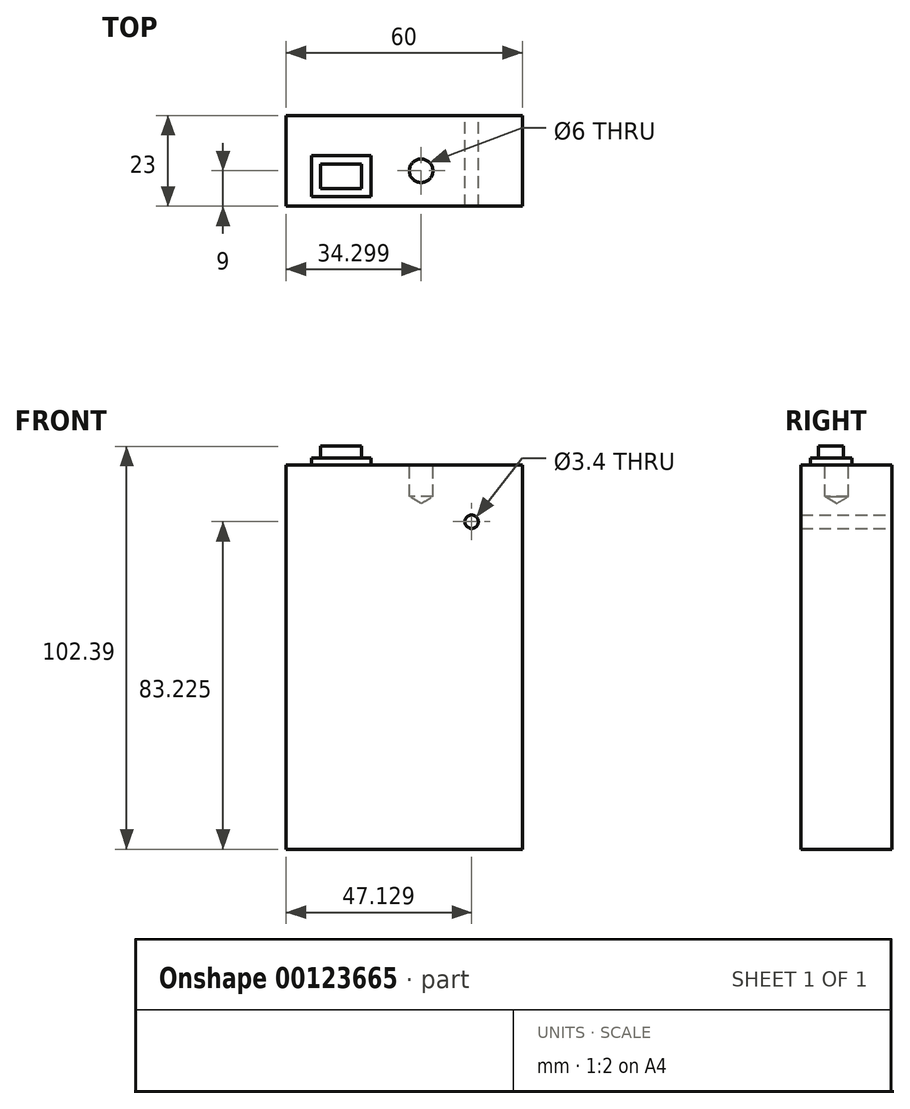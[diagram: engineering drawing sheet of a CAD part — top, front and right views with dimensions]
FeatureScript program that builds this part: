
annotation { "Feature Type Name" : "Feature", "Feature Type Description" : "" }
export const myFeature = defineFeature(function(context is Context, id is Id, definition is map)
    precondition{}
    {
        {
            var Q0;
            Q0=qCreatedBy(makeId("Front.planeOp"),FACE);
            var sketch = newSketch(context, id + "F0", { "sketchPlane" : qUnion([Q0])});
            skLineSegment(sketch, "E0.bottom", {"start": v(-29.03, 63.6) * mm, "end": v(30.97, 63.6) * mm});
            skLineSegment(sketch, "E0.top", {"start": v(-29.03, -34.05) * mm, "end": v(30.97, -34.05) * mm});
            skLineSegment(sketch, "E0.left", {"start": v(-29.03, 63.6) * mm, "end": v(-29.03, -34.05) * mm});
            skLineSegment(sketch, "E0.right", {"start": v(30.97, 63.6) * mm, "end": v(30.97, -34.05) * mm});
            skCircle(sketch, "E1", {"center": v(18.1, 49.17) * mm, "radius": 1.7 * mm});
            skSolve(sketch);
        }
        {
            var Q0;
            Q0 = qSketchRegion(id + "F0", true);
            extrude(context, id + "F1", {"entities" : qUnion([Q0]), "depth" : 23 * mm});
        }
        {
            var Q0;
            Q0=makeQuery(id+"F1.opExtrude","SWEPT_FACE",FACE,{"disambiguationData":[OSD([sQuery(id+"F0.wireOp",EDGE,"E0.bottom")])]});
            var sketch = newSketch(context, id + "F2", { "sketchPlane" : qUnion([Q0])});
            skCircle(sketch, "E2", {"center": v(5.27, -14) * mm, "radius": 3 * mm});
            skLineSegment(sketch, "E3.bottom", {"start": v(-22.56, -10.16) * mm, "end": v(-7.43, -10.16) * mm});
            skLineSegment(sketch, "E3.top", {"start": v(-22.56, -20.6) * mm, "end": v(-7.43, -20.6) * mm});
            skLineSegment(sketch, "E3.left", {"start": v(-22.56, -10.16) * mm, "end": v(-22.56, -20.6) * mm});
            skLineSegment(sketch, "E3.right", {"start": v(-7.43, -10.16) * mm, "end": v(-7.43, -20.6) * mm});
            skLineSegment(sketch, "E4.bottom", {"start": v(-20.34, -12.25) * mm, "end": v(-9.84, -12.25) * mm});
            skLineSegment(sketch, "E4.top", {"start": v(-20.34, -18.55) * mm, "end": v(-9.84, -18.55) * mm});
            skLineSegment(sketch, "E4.left", {"start": v(-20.34, -12.25) * mm, "end": v(-20.34, -18.55) * mm});
            skLineSegment(sketch, "E4.right", {"start": v(-9.84, -12.25) * mm, "end": v(-9.84, -18.55) * mm});
            skSolve(sketch);
        }
        {
            var Q0;
            Q0=sQuery(id+"F2.wireOp",VERTEX,"E2.center");
            var Q1;
            Q1=makeQuery(id+"F1.opExtrude","SWEPT_BODY",BODY,{"disambiguationData":[OSD([sQuery(id+"F0.wireOp",EDGE,"E0.bottom"),sQuery(id+"F0.wireOp",EDGE,"E0.top"),sQuery(id+"F0.wireOp",EDGE,"E0.left"),sQuery(id+"F0.wireOp",EDGE,"E0.right")])]});
            hole(context, id + "F3", {"style" : HoleStyle.SIMPLE, "endStyle" : HoleEndStyle.BLIND, "holeDiameter" : 6 * mm, "holeDepth" : 8 * mm, "locations" : qUnion([Q0]), "scope" : qUnion([Q1])});
        }
        {
            var Q0;
            Q0=makeQuery(id+"F2.imprint","IMPRINT",FACE,{"disambiguationData":[TD([[makeQuery(id+"F2.imprint","IMPRINT",EDGE,{"derivedFrom":sQuery(id+"F2.wireOp",EDGE,"E4.bottom")}),-1.0]])]});
            extrude(context, id + "F4", {"entities" : qUnion([Q0]), "operationType" : NewBodyOperationType.ADD, "depth" : 4.75 * mm});
        }
        {
            var Q0;
            Q0=makeQuery(id+"F2.imprint","IMPRINT",FACE,{"disambiguationData":[TD([[makeQuery(id+"F2.imprint","IMPRINT",EDGE,{"derivedFrom":sQuery(id+"F2.wireOp",EDGE,"E3.bottom")}),-1.0]])]});
            extrude(context, id + "F5", {"entities" : qUnion([Q0]), "operationType" : NewBodyOperationType.ADD, "depth" : 1.75 * mm});
        }
    });
